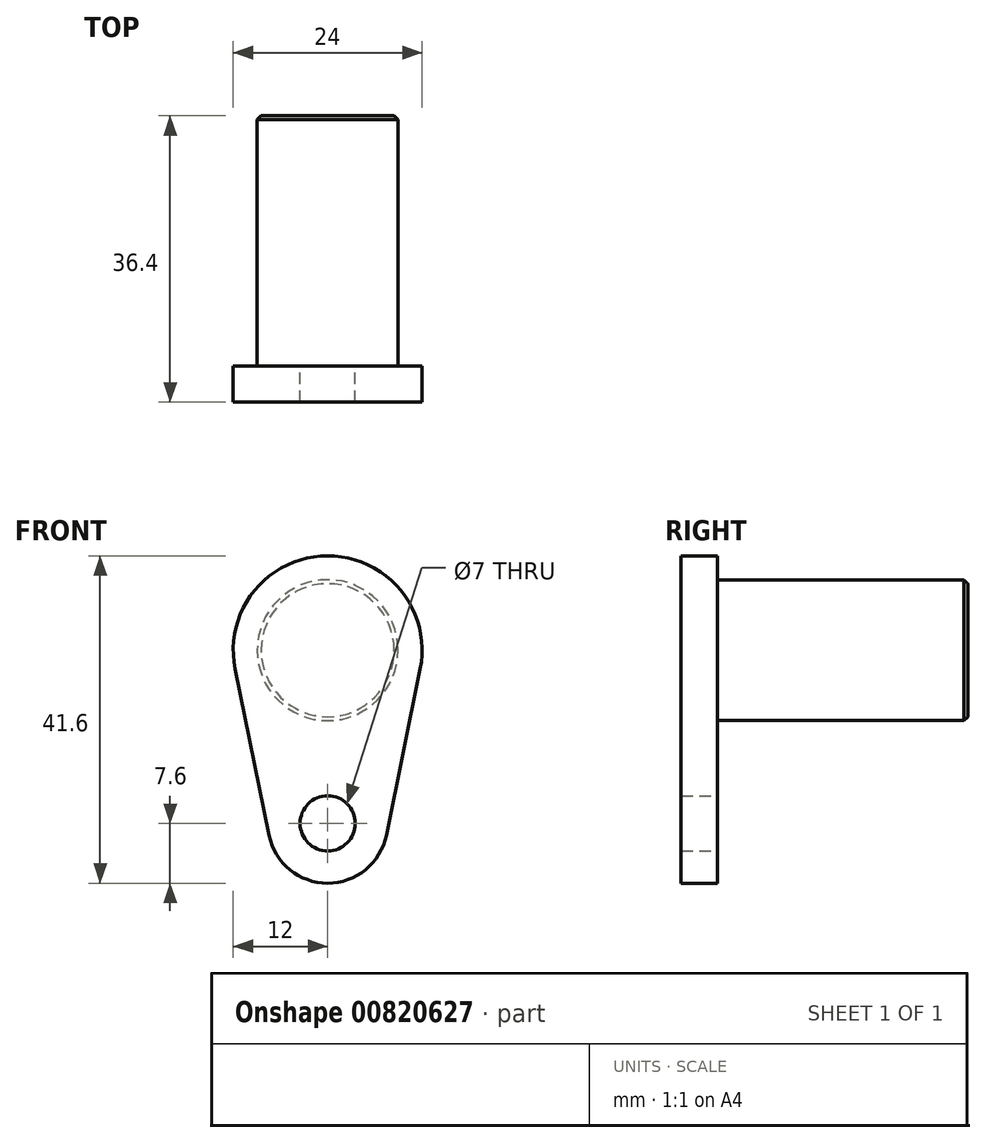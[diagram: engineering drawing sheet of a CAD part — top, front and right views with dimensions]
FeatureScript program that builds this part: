
annotation { "Feature Type Name" : "Feature", "Feature Type Description" : "" }
export const myFeature = defineFeature(function(context is Context, id is Id, definition is map)
    precondition{}
    {
        {
            var Q0;
            Q0=qCreatedBy(makeId("Front.planeOp"),FACE);
            var sketch = newSketch(context, id + "F0", { "sketchPlane" : qUnion([Q0])});
            skArc(sketch, "E0", {"start": v(11.76, -2.4) * mm, "mid": v(0, 12) * mm, "end": v(-11.76, -2.4) * mm});
            skArc(sketch, "E1", {"start": v(-7.45, -23.52) * mm, "mid": v(0, -29.6) * mm, "end": v(7.45, -23.52) * mm});
            skCircle(sketch, "E2", {"center": v(0, -22) * mm, "radius": 3.5 * mm});
            skLineSegment(sketch, "E3", {"start": v(-7.45, -23.52) * mm, "end": v(-11.76, -2.4) * mm});
            skLineSegment(sketch, "E4", {"start": v(7.45, -23.52) * mm, "end": v(11.76, -2.4) * mm});
            skPoint(sketch, "E5.orphan", {"position": v(-12.25, 0) * mm});
            skPoint(sketch, "E6.orphan", {"position": v(12.25, 0) * mm});
            skSolve(sketch);
        }
        {
            var Q0;
            Q0=makeQuery(id+"F0.imprint","IMPRINT",FACE,{"disambiguationData":[TD([[makeQuery(id+"F0.imprint","IMPRINT",EDGE,{"derivedFrom":sQuery(id+"F0.wireOp",EDGE,"E0")}),1.0]])]});
            extrude(context, id + "F1", {"entities" : qUnion([Q0]), "depth" : 4.6 * mm, "offsetDistance" : 25 * mm});
        }
        {
            var Q0;
            Q0=makeQuery(id+"F1.opExtrude","CAP_FACE",FACE,{"disambiguationData":[OSD([sQuery(id+"F0.wireOp",EDGE,"E0"),sQuery(id+"F0.wireOp",EDGE,"E1"),sQuery(id+"F0.wireOp",EDGE,"E2"),sQuery(id+"F0.wireOp",EDGE,"E3"),sQuery(id+"F0.wireOp",EDGE,"E4")])],"isStart":true});
            var sketch = newSketch(context, id + "F2", { "sketchPlane" : qUnion([Q0])});
            skCircle(sketch, "E7", {"center": v(0, 0) * mm, "radius": 8.95 * mm});
            skSolve(sketch);
        }
        {
            var Q0;
            Q0=makeQuery(id+"F2.imprint","IMPRINT",FACE,{"disambiguationData":[TD([[makeQuery(id+"F2.imprint","IMPRINT",EDGE,{"derivedFrom":sQuery(id+"F2.wireOp",EDGE,"E7")}),1.0]])]});
            extrude(context, id + "F3", {"entities" : qUnion([Q0]), "operationType" : NewBodyOperationType.ADD, "depth" : 31.8 * mm, "offsetDistance" : 25 * mm});
        }
        {
            var Q0;
            Q0=makeQuery(id+"F3.opExtrude","CAP_EDGE",EDGE,{"disambiguationData":[OSD([sQuery(id+"F2.wireOp",EDGE,"E7")])],"isStart":false});
            chamfer(context, id + "F4", {"entities" : qUnion([Q0]), "width" : .5 * mm, "tangentPropagation" : true});
        }
    });
